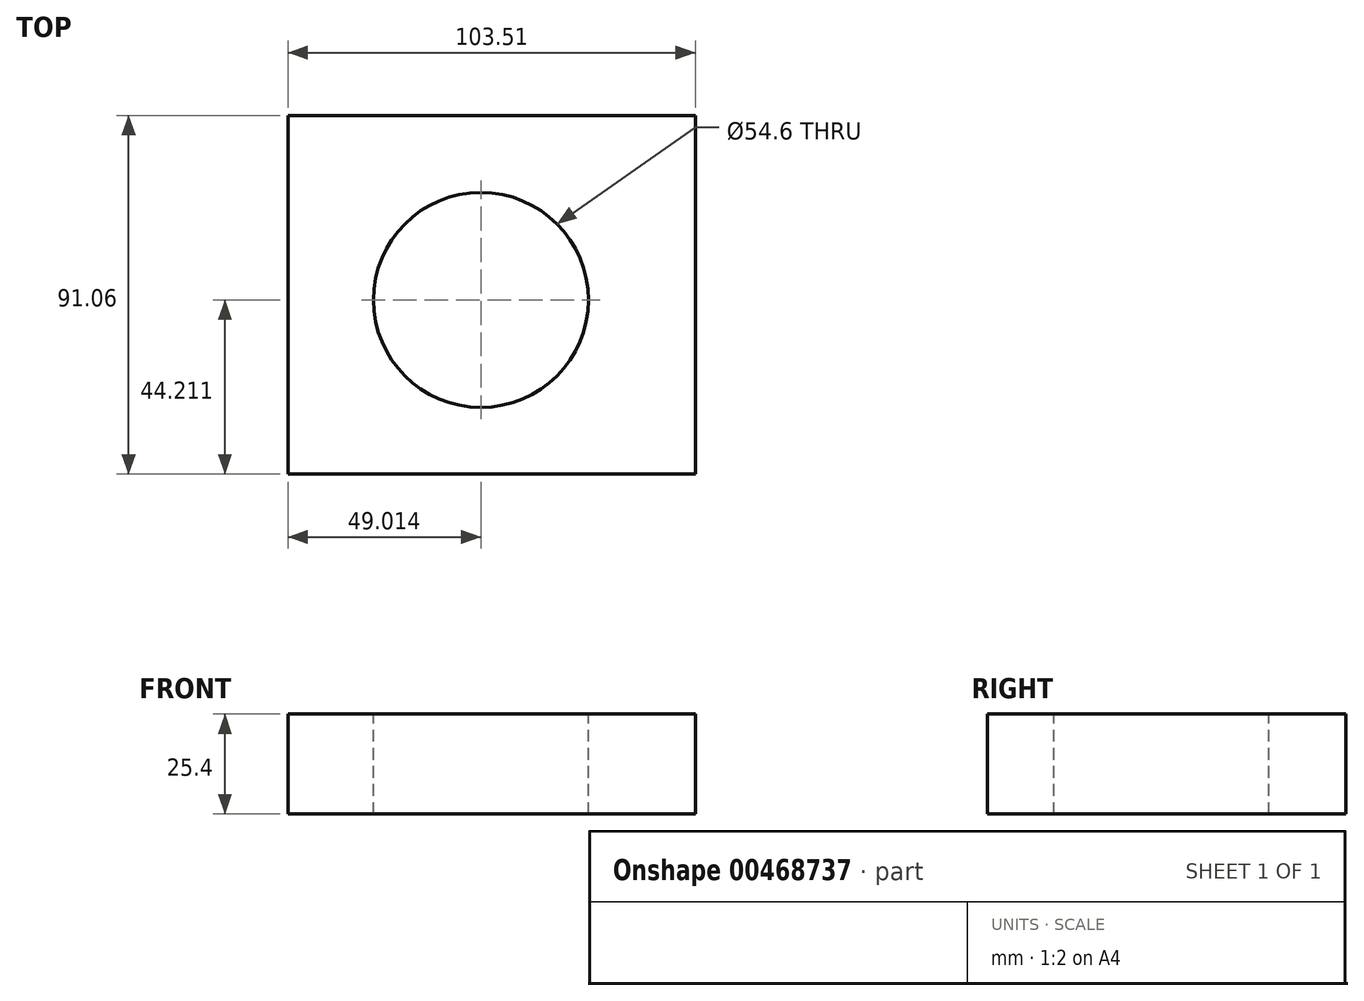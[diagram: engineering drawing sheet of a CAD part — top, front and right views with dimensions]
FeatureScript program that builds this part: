
annotation { "Feature Type Name" : "Feature", "Feature Type Description" : "" }
export const myFeature = defineFeature(function(context is Context, id is Id, definition is map)
    precondition{}
    {
        {
            var Q0;
            Q0=qCreatedBy(makeId("Top.planeOp"),FACE);
            var sketch = newSketch(context, id + "F0", { "sketchPlane" : qUnion([Q0])});
            skLineSegment(sketch, "E0.bottom", {"start": v(-56.32, -38.7) * mm, "end": v(47.2, -38.7) * mm});
            skLineSegment(sketch, "E0.top", {"start": v(-56.32, 52.37) * mm, "end": v(47.2, 52.37) * mm});
            skLineSegment(sketch, "E0.left", {"start": v(-56.32, -38.7) * mm, "end": v(-56.32, 52.37) * mm});
            skLineSegment(sketch, "E0.right", {"start": v(47.2, -38.7) * mm, "end": v(47.2, 52.37) * mm});
            skSolve(sketch);
        }
        {
            var Q0;
            Q0=qSketchRegion(id+"F0",true);
            extrude(context, id + "F1", {"entities" : qUnion([Q0]), "depth" : 25.4 * mm});
        }
        {
            var Q0;
            Q0=makeQuery(id+"F1.opExtrude","CAP_FACE",FACE,{"disambiguationData":[OSD([sQuery(id+"F0.wireOp",EDGE,"E0.bottom"),sQuery(id+"F0.wireOp",EDGE,"E0.top"),sQuery(id+"F0.wireOp",EDGE,"E0.left"),sQuery(id+"F0.wireOp",EDGE,"E0.right")])],"isStart":false});
            var sketch = newSketch(context, id + "F2", { "sketchPlane" : qUnion([Q0])});
            skCircle(sketch, "E1", {"center": v(-7.3, 5.52) * mm, "radius": 27.3 * mm});
            skSolve(sketch);
        }
        {
            var Q0;
            Q0=makeQuery(id+"F2.imprint","IMPRINT",FACE,{"disambiguationData":[TD([[makeQuery(id+"F2.imprint","IMPRINT",EDGE,{"derivedFrom":sQuery(id+"F2.wireOp",EDGE,"E1")}),1.0]])]});
            extrude(context, id + "F3", {"entities" : qUnion([Q0]), "operationType" : NewBodyOperationType.REMOVE, "endBound" : BoundingType.THROUGH_ALL, "oppositeDirection" : true, "depth" : 25.4 * mm});
        }
    });
